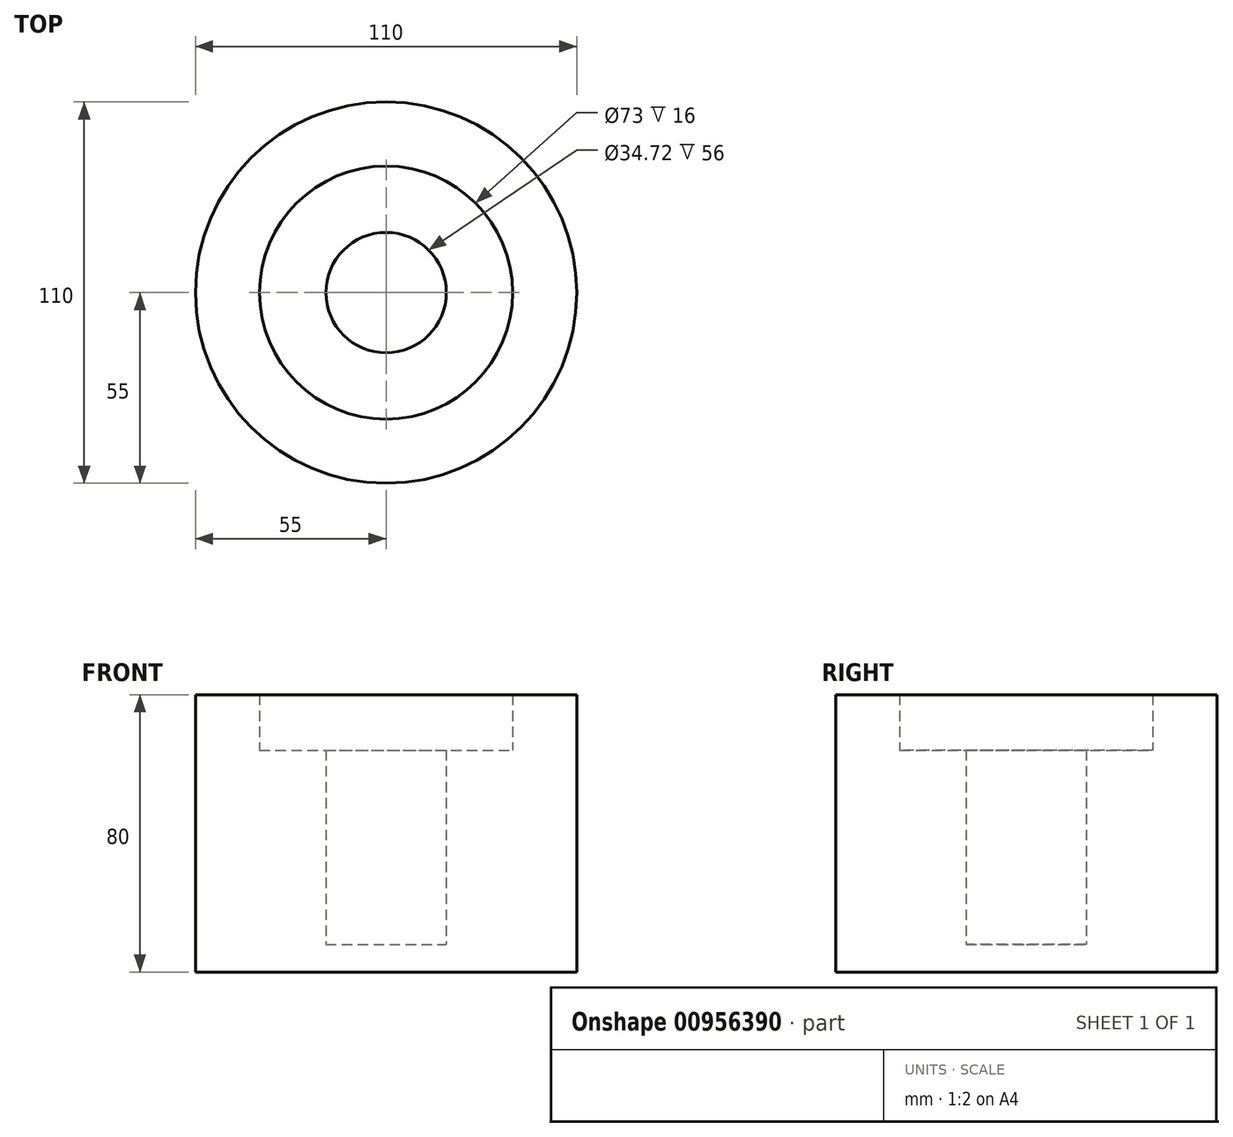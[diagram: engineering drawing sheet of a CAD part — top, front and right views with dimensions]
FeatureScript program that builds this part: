
annotation { "Feature Type Name" : "Feature", "Feature Type Description" : "" }
export const myFeature = defineFeature(function(context is Context, id is Id, definition is map)
    precondition{}
    {
        {
            var Q0;
            Q0=qCreatedBy(makeId("Front.planeOp"),FACE);
            var sketch = newSketch(context, id + "F0", { "sketchPlane" : qUnion([Q0])});
            skLineSegment(sketch, "E0", {"start": v(0, 0) * mm, "end": v(0, 83.05) * mm, "construction": true});
            skLineSegment(sketch, "E1", {"start": v(0, 3.31) * mm, "end": v(55, 3.31) * mm});
            skLineSegment(sketch, "E2", {"start": v(55, 3.31) * mm, "end": v(55, 83.31) * mm});
            skLineSegment(sketch, "E3", {"start": v(55, 83.31) * mm, "end": v(36.5, 83.31) * mm});
            skLineSegment(sketch, "E4", {"start": v(36.5, 83.31) * mm, "end": v(36.5, 67.31) * mm});
            skLineSegment(sketch, "E5", {"start": v(36.5, 67.31) * mm, "end": v(17.36, 67.31) * mm});
            skLineSegment(sketch, "E6", {"start": v(17.36, 67.31) * mm, "end": v(17.36, 11.31) * mm});
            skLineSegment(sketch, "E7", {"start": v(17.36, 11.31) * mm, "end": v(0, 11.31) * mm});
            skLineSegment(sketch, "E8", {"start": v(0, 11.31) * mm, "end": v(0, 3.31) * mm});
            skSolve(sketch);
        }
        {
            var Q0;
            Q0=makeQuery(id+"F0.imprint","IMPRINT",FACE,{"disambiguationData":[TD([[makeQuery(id+"F0.imprint","IMPRINT",EDGE,{"derivedFrom":sQuery(id+"F0.wireOp",EDGE,"E1")}),1.0]])]});
            var Q1;
            Q1=sQuery(id+"F0.wireOp",EDGE,"E0");
            revolve(context, id + "F1", {"surfaceOperationType" : NewSurfaceOperationType.NEW, "entities" : qUnion([Q0]), "axis" : qUnion([Q1]), "revolveType" : RevolveType.FULL});
        }
    });
